# Revit family: PolyMax-WallPanel
name_source: partatom
category: Specialty Equipment
units: mm (PartAtom-declared; Revit-internal decimal feet)

## family parameters
Always vertical = Yes
Classification Number = 23.35.17.20
Cut with Voids When Loaded = No
Enable Cutting in Views = No
Host = Wall
Maintain Annotation Orientation = No
Part Type = Normal
Room Calculation Point = No
Round Connector Dimension = Use Diameter
Shared = No

## types (4) — shared parameters
Assembly Code = F1030100
CSI No. = 09840
Default Elevation = 0' - 0"
Depth = 0' - 1"
Description = Acoustical Wall & Ceiling Tiles
Height = 8' - 0"
Height Above Floor = 4' - 0"
Keynote = 09800
Manufacturer = Acoustical Surfaces Inc.
Material = Acoustical Surfaces - White
Model = Poly Max™ Polyester Acoustical Panels
NRC = 0.7
URL = http://www.acousticalsurfaces.com
Width = 4' - 0"
zero-valued in all types: Cost, Expected Lifespan (Years), Maintenance Schedule (Months), Warranty Duration (Years)

## type names (no varying parameters)
- 1_4'x8'-Vertical
- 1_4'x8'-Horizontal
- 1_2'x4'-Horizontal
- 1_2'x4'-Vertical

## geometry (parser evidence)
native form markers: Sweep x1
no freeform markers — native parametric forms only
